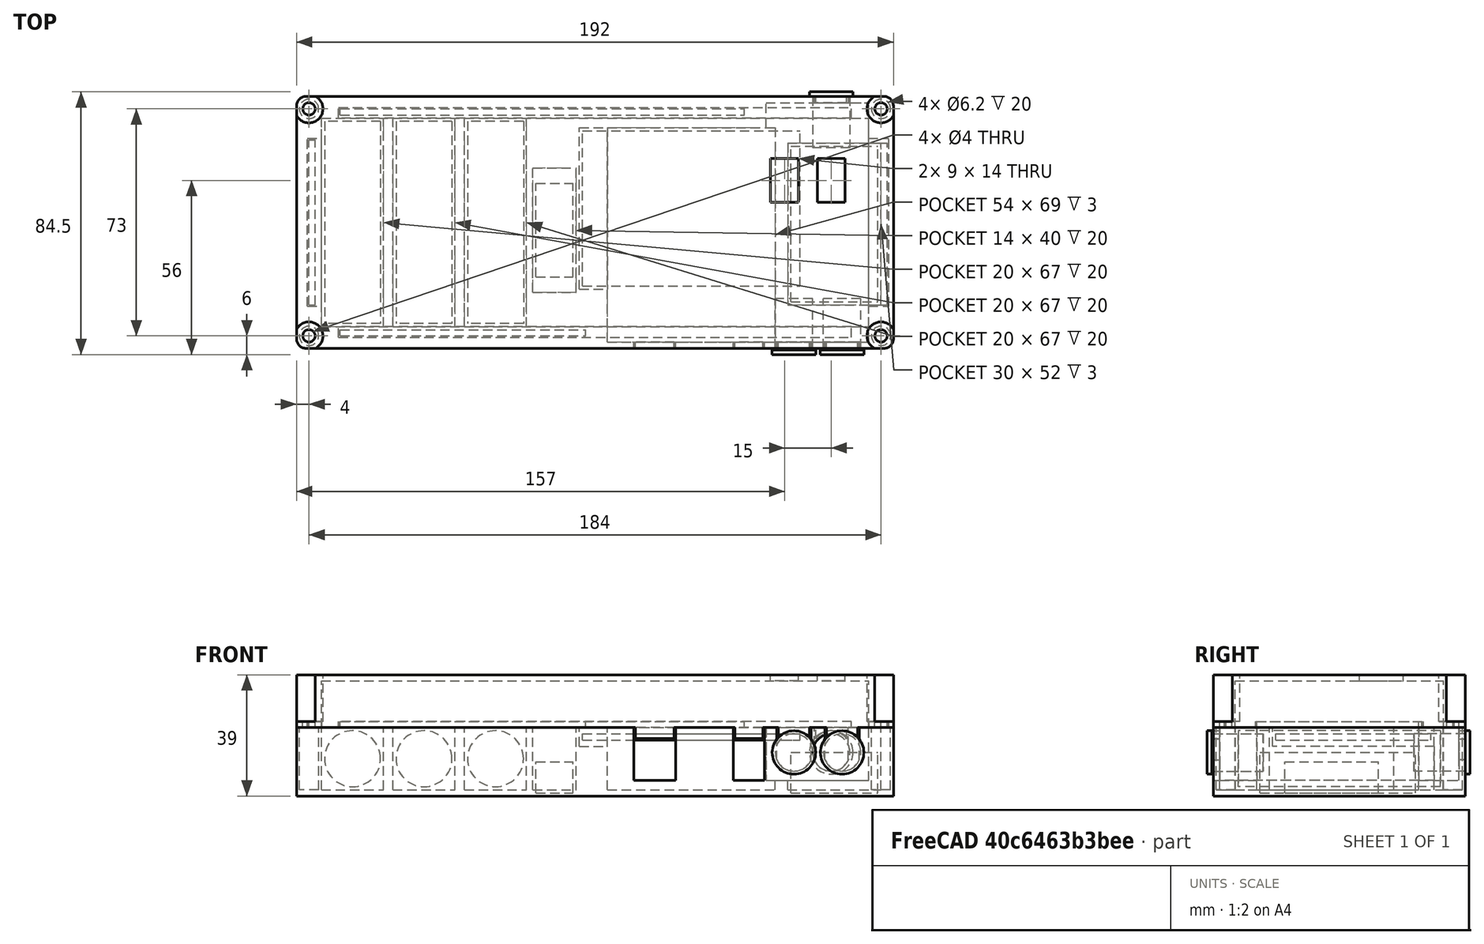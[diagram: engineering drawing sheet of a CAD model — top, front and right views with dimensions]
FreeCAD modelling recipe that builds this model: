
FCSTD DOCUMENT  (FreeCAD 0.19R24366 (Git))
Label: OpenBatteryPack_pt1
License: All rights reserved
LicenseURL: http://en.wikipedia.org/wiki/All_rights_reserved
objects: Part::Box×38, Part::Cylinder×30, Part::MultiFuse×17, Part::Cut×13, Part::Compound×3, Part::Fillet×2, Mesh::Feature×1
note: 103 computed .brp shape members not serialized (recipe doc carries the construction recipe); baked Part::Feature solids carry a one-line shape summary decoded from their .brp

FEATURE [Part::Box] Box  label="MainVolume"
  AttacherType = Attacher::AttachEngine3D
  Height = 22
  Length = 192
  Placement = pos=(-2,0,-1) rot=(0,0,1;0rad)
  Width = 81
FEATURE [Part::Cylinder] Cylinder  label="18650 Battery"
  Angle = 360
  AttacherType = Attacher::AttachEngine3D
  Height = 65
  Placement = pos=(16,73,11) rot=(1,0,0;1.5708rad)
  Radius = 9
FEATURE [Part::Cylinder] Cylinder001  label="18650 Battery001"
  Angle = 360
  AttacherType = Attacher::AttachEngine3D
  Height = 65
  Placement = pos=(39,73,11) rot=(1,0,0;1.5708rad)
  Radius = 9
FEATURE [Part::Cylinder] Cylinder002  label="18650 Battery002"
  Angle = 360
  AttacherType = Attacher::AttachEngine3D
  Height = 65
  Placement = pos=(62,73,11) rot=(1,0,0;1.5708rad)
  Radius = 9
FEATURE [Mesh::Feature] Arduino_ipt  label="Arduino.ipt"
  Placement = pos=(160,28,36) rot=(0,0,1;0rad)
FEATURE [Part::Box] Box001  label="Main Board"
  AttacherType = Attacher::AttachEngine3D
  Height = 2
  Length = 70
  Placement = pos=(90,20,17) rot=(0,0,1;0rad)
  Width = 50
FEATURE [Part::Box] Box002  label="Current Sensor"
  AttacherType = Attacher::AttachEngine3D
  Height = 10
  Length = 12
  Placement = pos=(75,23,0) rot=(0,0,1;0rad)
  Width = 30
FEATURE [Part::Cylinder] Cylinder003  label="Cylinder"
  Angle = 360
  AttacherType = Attacher::AttachEngine3D
  Height = 18
  Radius = 6
FEATURE [Part::Cylinder] Cylinder004
  Angle = 360
  AttacherType = Attacher::AttachEngine3D
  Height = 1.5
  Radius = 7
FEATURE [Part::MultiFuse] Fusion  label="DC Jack"
  Placement = pos=(173.5,-2,13) rot=(1,0,0;-1.5708rad)
  Shapes = -> [Cylinder003,Cylinder004]
FEATURE [Part::Cylinder] Cylinder005
  Angle = 360
  AttacherType = Attacher::AttachEngine3D
  Height = 18
  Radius = 6
FEATURE [Part::Cylinder] Cylinder006
  Angle = 360
  AttacherType = Attacher::AttachEngine3D
  Height = 1.5
  Radius = 7
FEATURE [Part::MultiFuse] Fusion001  label="DC Jack001"
  Placement = pos=(158,-2,13) rot=(1,0,0;-1.5708rad)
  Shapes = -> [Cylinder005,Cylinder006]
FEATURE [Part::Cylinder] Cylinder007
  Angle = 360
  AttacherType = Attacher::AttachEngine3D
  Height = 18
  Radius = 6
FEATURE [Part::Cylinder] Cylinder008
  Angle = 360
  AttacherType = Attacher::AttachEngine3D
  Height = 1.5
  Radius = 7
FEATURE [Part::MultiFuse] Fusion002  label="DC Jack002"
  Placement = pos=(170,82.5,13) rot=(-1,0,0;-1.5708rad)
  Shapes = -> [Cylinder007,Cylinder008]
FEATURE [Part::Box] Box003  label="DC-DC Step Up"
  AttacherType = Attacher::AttachEngine3D
  Height = 13
  Length = 28
  Placement = pos=(157,15,0) rot=(0,0,1;0rad)
  Width = 50
FEATURE [Part::Cylinder] Cylinder009  label="M4 Mounting Hole"
  Angle = 360
  AttacherType = Attacher::AttachEngine3D
  Height = 20
  Placement = pos=(2,4,1) rot=(0,0,1;0rad)
  Radius = 3.1
FEATURE [Part::Cylinder] Cylinder010  label="M4 Mounting Hole001"
  Angle = 360
  AttacherType = Attacher::AttachEngine3D
  Height = 20
  Placement = pos=(2,77,1) rot=(0,0,1;0rad)
  Radius = 3.1
FEATURE [Part::Cylinder] Cylinder011  label="M4 Mounting Hole002"
  Angle = 360
  AttacherType = Attacher::AttachEngine3D
  Height = 20
  Placement = pos=(186,77,1) rot=(0,0,1;0rad)
  Radius = 3.1
FEATURE [Part::Cylinder] Cylinder012  label="M4 Mounting Hole003"
  Angle = 360
  AttacherType = Attacher::AttachEngine3D
  Height = 20
  Placement = pos=(186,4,1) rot=(0,0,1;0rad)
  Radius = 3.1
FEATURE [Part::Box] Box004  label="18650 MNT PLACE"
  AttacherType = Attacher::AttachEngine3D
  Height = 20
  Length = 20
  Placement = pos=(6,7,1) rot=(0,0,1;0rad)
  Width = 67
FEATURE [Part::Box] Box005  label="18650 MNT PLACE001"
  AttacherType = Attacher::AttachEngine3D
  Height = 20
  Length = 20
  Placement = pos=(29,7,1) rot=(0,0,1;0rad)
  Width = 67
FEATURE [Part::Box] Box006  label="18650 MNT PLACE002"
  AttacherType = Attacher::AttachEngine3D
  Height = 20
  Length = 20
  Placement = pos=(52,7,1) rot=(0,0,1;0rad)
  Width = 67
FEATURE [Part::Box] Box007  label="Current Sensor MNT Place"
  AttacherType = Attacher::AttachEngine3D
  Height = 20
  Length = 14
  Placement = pos=(74,18,1) rot=(0,0,1;0rad)
  Width = 40
FEATURE [Part::Box] Box008  label="Arduino MNT Place"
  AttacherType = Attacher::AttachEngine3D
  Height = 20
  Length = 54
  Placement = pos=(98,2,1) rot=(0,0,1;0rad)
  Width = 69
FEATURE [Part::Box] Box009  label="DC-DC Step Up MNT Place"
  AttacherType = Attacher::AttachEngine3D
  Height = 20
  Length = 30
  Placement = pos=(156,14,1) rot=(0,0,1;0rad)
  Width = 52
FEATURE [Part::Box] Box010  label="Main Board MNT Place"
  AttacherType = Attacher::AttachEngine3D
  Height = 6
  Length = 72
  Placement = pos=(89,19,15) rot=(0,0,1;0rad)
  Width = 52
FEATURE [Part::MultiFuse] Fusion003  label="Inner MNT Holes"
  Shapes = -> [Cylinder009,Cylinder010,Cylinder011,Cylinder012,Box004,Box005,Box006,Box007,Box008,Box009,Box010]
FEATURE [Part::Cut] Cut
  Base = -> Box
  Tool = -> Fusion003
FEATURE [Part::Box] Box011  label="Arduino USB-B Hole"
  AttacherType = Attacher::AttachEngine3D
  Height = 21
  Length = 13.5
  Placement = pos=(106.5,-1,4) rot=(0,0,1;0rad)
  Width = 11
FEATURE [Part::Box] Box012  label="Arduion DC-IN Hole"
  AttacherType = Attacher::AttachEngine3D
  Height = 21
  Length = 10
  Placement = pos=(138.5,-1,4) rot=(0,0,1;0rad)
  Width = 11
FEATURE [Part::MultiFuse] Fusion004  label="Arduino Jacks Holes"
  Shapes = -> [Box011,Box012]
FEATURE [Part::Cut] Cut001
  Base = -> Cut
  Tool = -> Fusion004
FEATURE [Part::Box] Box013  label="Cube"
  AttacherType = Attacher::AttachEngine3D
  Height = 17
  Length = 33
  Placement = pos=(149,2,4) rot=(0,0,1;0rad)
  Width = 77
FEATURE [Part::Cut] Cut002
  Base = -> Cut001
  Tool = -> Box013
FEATURE [Part::Cylinder] Cylinder013
  Angle = 360
  AttacherType = Attacher::AttachEngine3D
  Height = 18
  Radius = 6
FEATURE [Part::Cylinder] Cylinder014
  Angle = 360
  AttacherType = Attacher::AttachEngine3D
  Height = 1.5
  Radius = 7
FEATURE [Part::MultiFuse] Fusion005  label="DC Jack_Hole_1"
  Placement = pos=(173.5,-2,13) rot=(-1,0,0;1.5708rad)
  Shapes = -> [Cylinder013,Cylinder014]
FEATURE [Part::Cylinder] Cylinder015
  Angle = 360
  AttacherType = Attacher::AttachEngine3D
  Height = 18
  Radius = 6
FEATURE [Part::Cylinder] Cylinder016
  Angle = 360
  AttacherType = Attacher::AttachEngine3D
  Height = 1.5
  Radius = 7
FEATURE [Part::MultiFuse] Fusion006  label="DC Jack_Hole_2"
  Placement = pos=(158,-2,13) rot=(-1,0,0;1.5708rad)
  Shapes = -> [Cylinder015,Cylinder016]
FEATURE [Part::Cylinder] Cylinder017
  Angle = 360
  AttacherType = Attacher::AttachEngine3D
  Height = 18
  Radius = 6
FEATURE [Part::Cylinder] Cylinder018
  Angle = 360
  AttacherType = Attacher::AttachEngine3D
  Height = 1.5
  Radius = 7
FEATURE [Part::MultiFuse] Fusion007  label="DC Jack_Hole_3"
  Placement = pos=(170,82.5,13) rot=(1,0,0;1.5708rad)
  Shapes = -> [Cylinder017,Cylinder018]
FEATURE [Part::MultiFuse] Fusion008  label="DC_Jack_Holes"
  Shapes = -> [Fusion005,Fusion006,Fusion007]
FEATURE [Part::Cut] Cut003
  Base = -> Cut002
  Tool = -> Fusion008
FEATURE [Part::Box] Box014  label="Cube001"
  AttacherType = Attacher::AttachEngine3D
  Height = 20
  Length = 12
  Placement = pos=(152,0,13) rot=(0,0,1;0rad)
  Width = 10
FEATURE [Part::Box] Box015  label="Cube002"
  AttacherType = Attacher::AttachEngine3D
  Height = 20
  Length = 12
  Placement = pos=(167.5,0,13) rot=(0,0,1;0rad)
  Width = 10
FEATURE [Part::Box] Box016  label="Cube003"
  AttacherType = Attacher::AttachEngine3D
  Height = 20
  Length = 12
  Placement = pos=(164,71,13) rot=(0,0,1;0rad)
  Width = 10
FEATURE [Part::MultiFuse] Fusion009  label="DC-DC MNT Holes_1"
  Shapes = -> [Box014,Box015,Box016]
FEATURE [Part::Cut] Cut004
  Base = -> Cut003
  Tool = -> Fusion009
FEATURE [Part::Fillet] Fillet
  Base = -> Cut004
  Edges = 4 edges r=3: [Edge1,Edge3,Edge23,Edge53]
FEATURE [Part::Box] Box017  label="Cube004"
  AttacherType = Attacher::AttachEngine3D
  Height = 12
  Length = 0.5
  Placement = pos=(152,0,9) rot=(0,0,1;0rad)
  Width = 2
FEATURE [Part::Box] Box018  label="Cube005"
  AttacherType = Attacher::AttachEngine3D
  Height = 12
  Length = 0.5
  Placement = pos=(163.5,0,9) rot=(0,0,1;0rad)
  Width = 2
FEATURE [Part::Box] Box019  label="Cube006"
  AttacherType = Attacher::AttachEngine3D
  Height = 12
  Length = 0.5
  Placement = pos=(167.5,0,9) rot=(0,0,1;0rad)
  Width = 2
FEATURE [Part::Box] Box020  label="Cube007"
  AttacherType = Attacher::AttachEngine3D
  Height = 12
  Length = 0.5
  Placement = pos=(179,0,9) rot=(0,0,1;0rad)
  Width = 2
FEATURE [Part::Box] Box021  label="Cube008"
  AttacherType = Attacher::AttachEngine3D
  Height = 12
  Length = 0.5
  Placement = pos=(175.5,79,9) rot=(0,0,1;0rad)
  Width = 2
FEATURE [Part::Box] Box022  label="Cube009"
  AttacherType = Attacher::AttachEngine3D
  Height = 12
  Length = 0.5
  Placement = pos=(164,79,9) rot=(0,0,1;0rad)
  Width = 2
FEATURE [Part::MultiFuse] Fusion010  label="NarrowingDCJackMounts"
  Shapes = -> [Box017,Box018,Box019,Box020,Box021,Box022]
FEATURE [Part::MultiFuse] Fusion011  label="Body_No_Latch"
  Shapes = -> [Fillet,Fusion010]
FEATURE [Part::Box] Box023  label="Cube010"
  AttacherType = Attacher::AttachEngine3D
  Height = 2
  Length = 2
  Placement = pos=(2,14,21) rot=(0,0,1;0rad)
  Width = 53
FEATURE [Part::Box] Box024  label="Cube011"
  AttacherType = Attacher::AttachEngine3D
  Height = 2
  Length = 130
  Placement = pos=(12,75,21) rot=(0,0,1;0rad)
  Width = 2
FEATURE [Part::Box] Box025  label="Cube012"
  AttacherType = Attacher::AttachEngine3D
  Height = 2
  Length = 79
  Placement = pos=(12,4,21) rot=(0,0,1;0rad)
  Width = 2
FEATURE [Part::Box] Box026  label="Cube013"
  AttacherType = Attacher::AttachEngine3D
  Height = 2
  Length = 2
  Placement = pos=(186,14,21) rot=(0,0,1;0rad)
  Width = 52
FEATURE [Part::Compound] Compound  label="Latches"
  Links = -> [Box023,Box024,Box025,Box026]
FEATURE [Part::MultiFuse] Fusion012  label="Body"
  Shapes = -> [Fusion011,Compound]
FEATURE [Part::Box] Box027  label="Cover Main Volume"
  AttacherType = Attacher::AttachEngine3D
  Height = 17
  Length = 192
  Placement = pos=(-2,0,21) rot=(0,0,1;0rad)
  Width = 81
FEATURE [Part::Fillet] Fillet001
  Base = -> Box027
  Edges = 4 edges r=3: [Edge1,Edge3,Edge5,Edge7]
FEATURE [Part::Box] Box028  label="Cube014"
  AttacherType = Attacher::AttachEngine3D
  Height = 2
  Length = 187
  Placement = pos=(1.5,13.5,21) rot=(0,0,1;0rad)
  Width = 54
FEATURE [Part::Box] Box029  label="Cube015"
  AttacherType = Attacher::AttachEngine3D
  Height = 2
  Length = 165
  Placement = pos=(11.5,3.5,21) rot=(0,0,1;0rad)
  Width = 74
FEATURE [Part::MultiFuse] Fusion013  label="LatchForCover"
  Shapes = -> [Box028,Box029]
FEATURE [Part::Cut] Cut005
  Base = -> Fillet001
  Tool = -> Fusion013
FEATURE [Part::Box] Box030  label="Cube016"
  AttacherType = Attacher::AttachEngine3D
  Height = 15
  Length = 176
  Placement = pos=(6,7,21) rot=(0,0,1;0rad)
  Width = 67
FEATURE [Part::Cut] Cut006
  Base = -> Cut005
  Tool = -> Box030
FEATURE [Part::Cylinder] Cylinder019
  Angle = 360
  AttacherType = Attacher::AttachEngine3D
  Height = 20
  Placement = pos=(2,4,0) rot=(0,0,1;0rad)
  Radius = 2
FEATURE [Part::Cylinder] Cylinder020
  Angle = 360
  AttacherType = Attacher::AttachEngine3D
  Height = 20
  Placement = pos=(2,77,0) rot=(0,0,1;0rad)
  Radius = 2
FEATURE [Part::Cylinder] Cylinder021
  Angle = 360
  AttacherType = Attacher::AttachEngine3D
  Height = 20
  Placement = pos=(186,77,0) rot=(0,0,1;0rad)
  Radius = 2
FEATURE [Part::Cylinder] Cylinder022
  Angle = 360
  AttacherType = Attacher::AttachEngine3D
  Height = 20
  Placement = pos=(186,4,0) rot=(0,0,1;0rad)
  Radius = 2
FEATURE [Part::MultiFuse] Fusion014
  Placement = pos=(0,0,18) rot=(0,0,1;0rad)
  Shapes = -> [Cylinder019,Cylinder020,Cylinder021,Cylinder022]
FEATURE [Part::Cut] Cut007
  Base = -> Cut006
  Tool = -> Fusion014
FEATURE [Part::Cylinder] Cylinder023
  Angle = 360
  AttacherType = Attacher::AttachEngine3D
  Height = 20
  Placement = pos=(2,77,0) rot=(0,0,1;0rad)
  Radius = 4.5
FEATURE [Part::Cylinder] Cylinder024
  Angle = 360
  AttacherType = Attacher::AttachEngine3D
  Height = 20
  Placement = pos=(186,77,0) rot=(0,0,1;0rad)
  Radius = 4.5
FEATURE [Part::Cylinder] Cylinder025
  Angle = 360
  AttacherType = Attacher::AttachEngine3D
  Height = 20
  Placement = pos=(186,4,0) rot=(0,0,1;0rad)
  Radius = 4.5
FEATURE [Part::Cylinder] Cylinder026
  Angle = 360
  AttacherType = Attacher::AttachEngine3D
  Height = 20
  Placement = pos=(2,4,0) rot=(0,0,1;0rad)
  Radius = 4.5
FEATURE [Part::MultiFuse] Fusion015
  Placement = pos=(0,0,23) rot=(0,0,1;0rad)
  Shapes = -> [Cylinder026,Cylinder023,Cylinder024,Cylinder025]
FEATURE [Part::Cut] Cut008
  Base = -> Cut007
  Tool = -> Fusion015
FEATURE [Part::Box] Box031  label="Switch Placement Hole"
  AttacherType = Attacher::AttachEngine3D
  Height = 10
  Length = 9
  Placement = pos=(165.5,47,31) rot=(0,0,1;0rad)
  Width = 14
FEATURE [Part::Box] Box032  label="Switch Placement Hole001"
  AttacherType = Attacher::AttachEngine3D
  Height = 10
  Length = 9
  Placement = pos=(150.5,47,31) rot=(0,0,1;0rad)
  Width = 14
FEATURE [Part::Compound] Compound001
  Links = -> [Box031,Box032]
FEATURE [Part::Cut] Cut009
  Base = -> Cut008
  Tool = -> Compound001
FEATURE [Part::Box] Box033  label="Cube017"
  AttacherType = Attacher::AttachEngine3D
  Height = 10
  Length = 12.5
  Placement = pos=(107,0,17.5) rot=(0,0,1;0rad)
  Width = 2
FEATURE [Part::Box] Box034  label="Cube018"
  AttacherType = Attacher::AttachEngine3D
  Height = 10
  Length = 9
  Placement = pos=(139,0,17.5) rot=(0,0,1;0rad)
  Width = 2
FEATURE [Part::Box] Box035  label="Cube019"
  AttacherType = Attacher::AttachEngine3D
  Height = 10
  Length = 10
  Placement = pos=(153,0,14.5) rot=(0,0,1;0rad)
  Width = 2
FEATURE [Part::Cylinder] Cylinder027
  Angle = 360
  AttacherType = Attacher::AttachEngine3D
  Height = 10
  Placement = pos=(158,-4,13) rot=(1,0,0;-1.5708rad)
  Radius = 6
FEATURE [Part::Cut] Cut010
  Base = -> Box035
  Placement = pos=(0,0,1) rot=(0,0,1;0rad)
  Tool = -> Cylinder027
FEATURE [Part::Box] Box036  label="Cube020"
  AttacherType = Attacher::AttachEngine3D
  Height = 10
  Length = 10
  Placement = pos=(153,0,14.5) rot=(0,0,1;0rad)
  Width = 2
FEATURE [Part::Cylinder] Cylinder028
  Angle = 360
  AttacherType = Attacher::AttachEngine3D
  Height = 10
  Placement = pos=(158,-4,13) rot=(-1,0,0;1.5708rad)
  Radius = 6
FEATURE [Part::Cut] Cut011
  Base = -> Box036
  Placement = pos=(12,79,1) rot=(0,0,1;0rad)
  Tool = -> Cylinder028
FEATURE [Part::Cylinder] Cylinder029
  Angle = 360
  AttacherType = Attacher::AttachEngine3D
  Height = 10
  Placement = pos=(158,-4,13) rot=(-1,0,0;1.5708rad)
  Radius = 6
FEATURE [Part::Box] Box037  label="Cube021"
  AttacherType = Attacher::AttachEngine3D
  Height = 10
  Length = 10
  Placement = pos=(153,0,14.5) rot=(0,0,1;0rad)
  Width = 2
FEATURE [Part::Cut] Cut012
  Base = -> Box037
  Placement = pos=(15.5,0,1) rot=(0,0,1;0rad)
  Tool = -> Cylinder029
FEATURE [Part::Compound] Compound002  label="CoverHoles"
  Links = -> [Box033,Box034,Cut010,Cut011,Cut012]
FEATURE [Part::MultiFuse] Fusion016  label="Cover"
  Shapes = -> [Cut009,Compound002]
